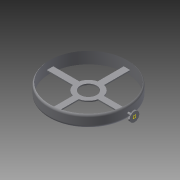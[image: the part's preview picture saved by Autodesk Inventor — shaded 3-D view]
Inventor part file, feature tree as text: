
AUTODESK INVENTOR PART (.ipt)
format: ipt  version: 2015 (Build 190159000, 159)  size: 244,224 bytes
history: native  units: in
note: dims shown in document units (in); Inventor stores cm internally (conversion verified against a paired STEP export)
features: extrude x9, sketch x6, fillet x3, plane x3, revolve x1, pattern_circular x1
ambient origin geometry x8: Origin, YZ Plane, XZ Plane, XY Plane, X Axis, Y Axis, Z Axis, Center Point
bodies: Solid1 (feature_tree)
feature tree (23):
  revolve  "Revolution1"  [1 undecoded]
  fillet  "Fillet1"  Radius=0.05in
  fillet  "Fillet2"  [1 undecoded]
  sketch  "Sketch2"  dims[d4=0.125in d5=0.125in]
  extrude  "Extrusion1"  Depth=0.125in
  extrude  "Extrusion2"  Depth=0.05in
  extrude  "Extrusion3"  Depth=1.0in TaperAngle=0.0deg
  extrude  "Extrusion4"  Depth=1.0in TaperAngle=0.0deg
  extrude  "Extrusion5"  Depth=0.05in TaperAngle=0.0deg
  plane  "Work Plane1"
  extrude  "Extrusion6"  Depth=0.05in
  fillet  "Fillet3"  Radius=1.0in
  plane  "Work Plane2"
  extrude  "Extrusion7"  Depth=0.05in
  plane  "Work Plane3"
  extrude  "Extrusion9"  Depth=0.05in
  extrude  "Extrusion10"  Depth=0.05in TaperAngle=0.0deg
  pattern_circular  "Circular Pattern1"  [2 undecoded]
  sketch  "Sketch1"  dims[d0=1.7in d1=0.5in d2=0.05in d3=90.0deg]
  sketch  "Sketch3"  dims[d6=0.05in d7=0.15in]
  sketch  "Sketch4"  dims[d9=0.5in d12=1.0in d13=0.0in]
  sketch  "Sketch6"  dims[d14=1.0in d15=0.0in d16=1.0in d17=0.0in]
  sketch  "Sketch7"  dims[d18=1.0in d19=0.0in d20=1.0in d21=0.0in d22=1.7in d24=1.0in d25=0.0in d26=0.04in d27=1.72in d29=1.0in d30=0.0in d32=0.095in d33=0.095in d37=0.13in d38=0.4in d39=0.24in d40=-0.3092in d41=0.05in d42=-0.2061in d43=2.3622in d44=360.0deg d54=0.7in d55=1.1in]
note: 4 required parameter values undecoded (feature->parameter linkage not recoverable at this tier; creation-order binding heuristic only, values carry confidence <= 0.55)